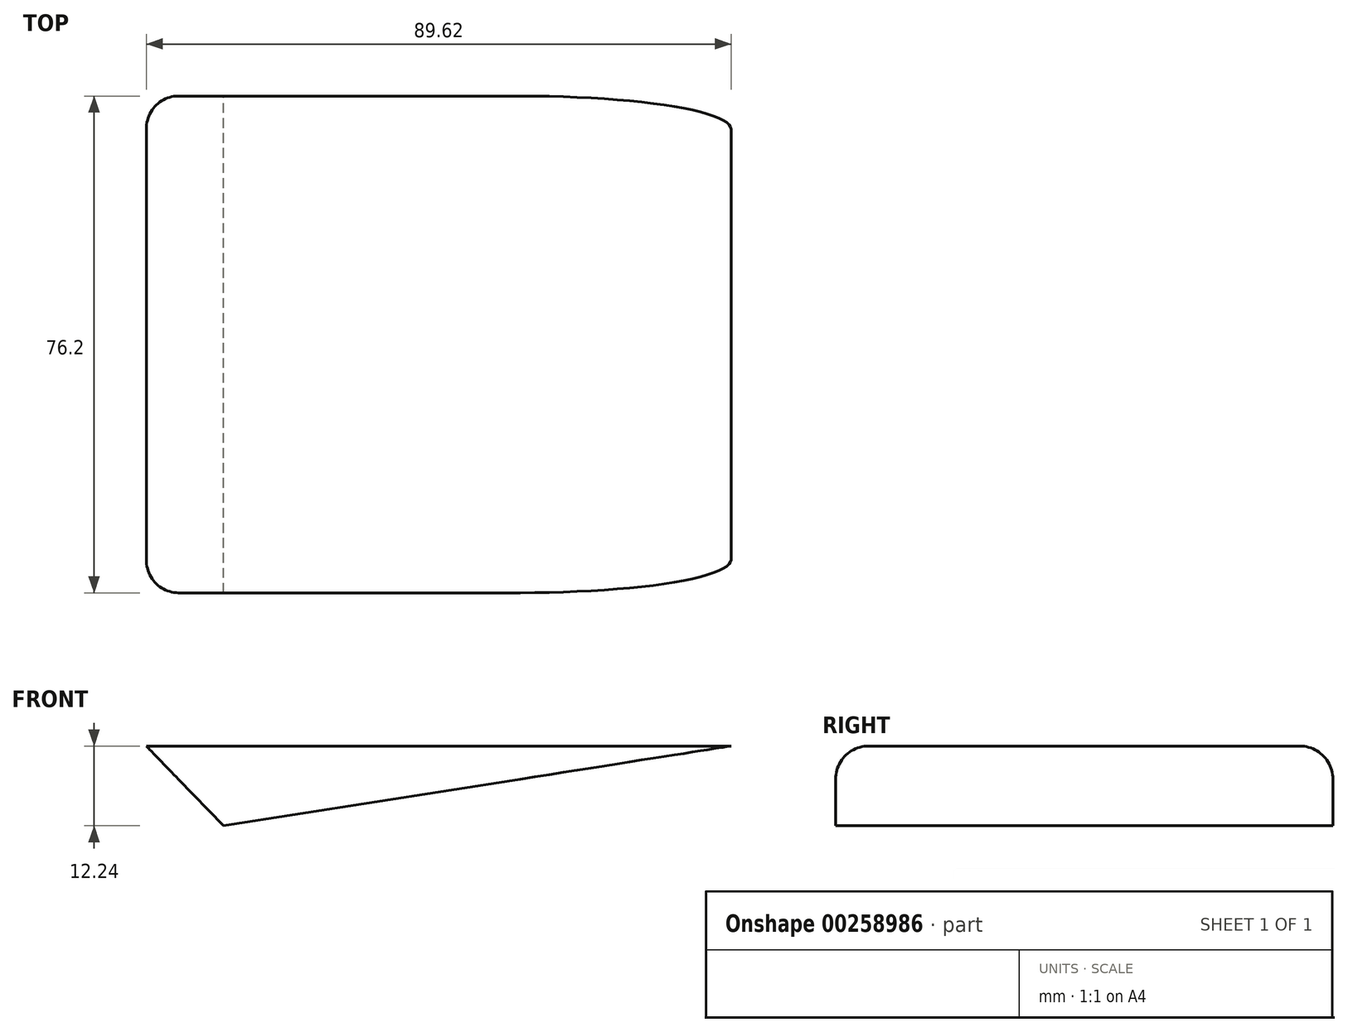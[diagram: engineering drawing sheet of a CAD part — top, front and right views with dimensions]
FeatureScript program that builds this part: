
annotation { "Feature Type Name" : "Feature", "Feature Type Description" : "" }
export const myFeature = defineFeature(function(context is Context, id is Id, definition is map)
    precondition{}
    {
        {
            var Q0;
            Q0=qCreatedBy(makeId("Front.planeOp"),FACE);
            var sketch = newSketch(context, id + "F0", { "sketchPlane" : qUnion([Q0])});
            skLineSegment(sketch, "E0", {"start": v(37.55, 19.3) * mm, "end": v(-52.07, 19.3) * mm});
            skLineSegment(sketch, "E1", {"start": v(-52.07, 19.3) * mm, "end": v(-40.25, 7.05) * mm});
            skLineSegment(sketch, "E2", {"start": v(-40.25, 7.05) * mm, "end": v(37.55, 19.3) * mm});
            skSolve(sketch);
        }
        {
            var Q0;
            Q0=makeQuery(id+"F0.imprint","IMPRINT",FACE,{"disambiguationData":[TD([[makeQuery(id+"F0.imprint","IMPRINT",EDGE,{"derivedFrom":sQuery(id+"F0.wireOp",EDGE,"E0")}),1.0]])]});
            extrude(context, id + "F1", {"entities" : qUnion([Q0]), "depth" : 76.2 * mm});
        }
        {
            var Q0;
            Q0=makeQuery(id+"F1.opExtrude","CAP_EDGE",EDGE,{"disambiguationData":[OSD([sQuery(id+"F0.wireOp",EDGE,"E0")])],"isStart":false});
            fillet(context, id + "F2", {"entities" : qUnion([Q0]), "radius" : 5.08 * mm, "tangentPropagation" : true, "allowEdgeOverflow" : false});
        }
        {
            var Q0;
            Q0=makeQuery(id+"F1.opExtrude","CAP_EDGE",EDGE,{"disambiguationData":[OSD([sQuery(id+"F0.wireOp",EDGE,"E0")])],"isStart":true});
            fillet(context, id + "F3", {"entities" : qUnion([Q0]), "radius" : 5.08 * mm, "tangentPropagation" : true, "allowEdgeOverflow" : false});
        }
    });
